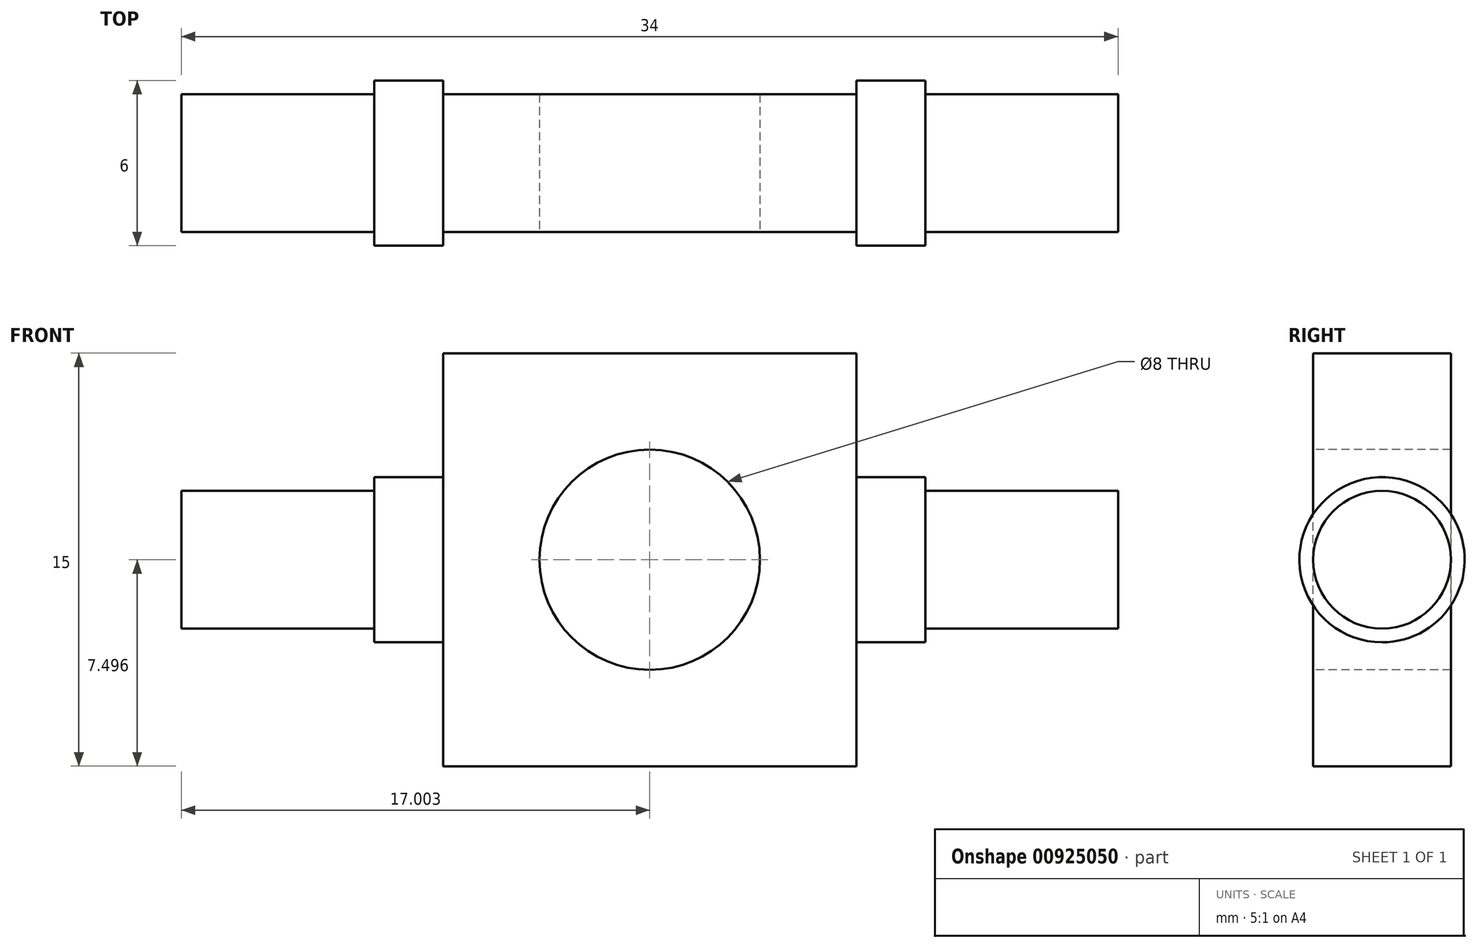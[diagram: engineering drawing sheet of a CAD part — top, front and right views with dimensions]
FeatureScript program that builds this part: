
annotation { "Feature Type Name" : "Feature", "Feature Type Description" : "" }
export const myFeature = defineFeature(function(context is Context, id is Id, definition is map)
    precondition{}
    {
        {
            var Q0;
            Q0=qCreatedBy(makeId("Front.planeOp"),FACE);
            var sketch = newSketch(context, id + "F0", { "sketchPlane" : qUnion([Q0])});
            skLineSegment(sketch, "E0.bottom", {"start": v(-9.98, 13.04) * mm, "end": v(5.02, 13.04) * mm});
            skLineSegment(sketch, "E0.top", {"start": v(-9.98, -1.96) * mm, "end": v(5.02, -1.96) * mm});
            skLineSegment(sketch, "E0.left", {"start": v(-9.98, 13.04) * mm, "end": v(-9.98, -1.96) * mm});
            skLineSegment(sketch, "E0.right", {"start": v(5.02, 13.04) * mm, "end": v(5.02, -1.96) * mm});
            skSolve(sketch);
        }
        {
            var Q0;
            Q0=makeQuery(id+"F0.imprint","IMPRINT",FACE,{"disambiguationData":[TD([[makeQuery(id+"F0.imprint","IMPRINT",EDGE,{"derivedFrom":sQuery(id+"F0.wireOp",EDGE,"E0.bottom")}),-1.0]])]});
            extrude(context, id + "F1", {"entities" : qUnion([Q0]), "depth" : 5 * mm, "offsetDistance" : 25 * mm});
        }
        {
            var Q0;
            Q0=makeQuery(id+"F1.opExtrude","CAP_FACE",FACE,{"disambiguationData":[OSD([sQuery(id+"F0.wireOp",EDGE,"E0.bottom"),sQuery(id+"F0.wireOp",EDGE,"E0.top"),sQuery(id+"F0.wireOp",EDGE,"E0.left"),sQuery(id+"F0.wireOp",EDGE,"E0.right")])],"isStart":false});
            var sketch = newSketch(context, id + "F2", { "sketchPlane" : qUnion([Q0])});
            skCircle(sketch, "E1", {"center": v(-2.48, 5.54) * mm, "radius": 4 * mm});
            skSolve(sketch);
        }
        {
            var Q0;
            Q0=makeQuery(id+"F2.imprint","IMPRINT",FACE,{"disambiguationData":[TD([[makeQuery(id+"F2.imprint","IMPRINT",EDGE,{"derivedFrom":sQuery(id+"F2.wireOp",EDGE,"E1")}),1.0]])]});
            extrude(context, id + "F3", {"entities" : qUnion([Q0]), "operationType" : NewBodyOperationType.REMOVE, "oppositeDirection" : true, "depth" : 25 * mm, "offsetDistance" : 25 * mm});
        }
        {
            var Q0;
            Q0=makeQuery(id+"F1.opExtrude","SWEPT_FACE",FACE,{"disambiguationData":[OSD([sQuery(id+"F0.wireOp",EDGE,"E0.right")])]});
            var sketch = newSketch(context, id + "F4", { "sketchPlane" : qUnion([Q0])});
            skCircle(sketch, "E2", {"center": v(-2.5, 5.54) * mm, "radius": 3 * mm});
            skSolve(sketch);
        }
        {
            var Q0;
            Q0 = qSketchRegion(id + "F4", true);
            extrude(context, id + "F5", {"entities" : qUnion([Q0]), "operationType" : NewBodyOperationType.ADD, "depth" : 2.5 * mm, "offsetDistance" : 25 * mm});
        }
        {
            var Q0;
            Q0=makeQuery(id+"F1.opExtrude","CAP_EDGE",EDGE,{"disambiguationData":[OSD([sQuery(id+"F0.wireOp",EDGE,"E0.bottom")])],"isStart":true});
            cPoint(context, id + "F6", {"entities" : qUnion([Q0]), "parameter" : 0.5});
        }
        {
            var Q0;
            Q0=makeQuery(id+"F1.opExtrude","CAP_EDGE",EDGE,{"disambiguationData":[OSD([sQuery(id+"F0.wireOp",EDGE,"E0.bottom")])],"isStart":false});
            cPoint(context, id + "F7", {"entities" : qUnion([Q0]), "parameter" : 0.5});
        }
        {
            var Q0;
            Q0=makeQuery(id+"F1.opExtrude","CAP_EDGE",EDGE,{"disambiguationData":[OSD([sQuery(id+"F0.wireOp",EDGE,"E0.top")])],"isStart":false});
            cPoint(context, id + "F8", {"entities" : qUnion([Q0]), "parameter" : 0.5});
        }
        {
            var Q0;
            Q0 = qCreatedBy(id + "F6" ,VERTEX);
            var Q1;
            Q1 = qCreatedBy(id + "F7" ,VERTEX);
            var Q2;
            Q2 = qCreatedBy(id + "F8" ,VERTEX);
            cPlane(context, id + "F9", {"entities" : qUnion([Q0, Q1, Q2]), "cplaneType" : CPlaneType.THREE_POINT, "offset" : 25 * mm, "width" : 150 * mm, "height" : 150 * mm});
        }
        {
            var Q0;
            Q0=makeQuery(id+"F5.opExtrude","CAP_FACE",FACE,{"disambiguationData":[OSD([sQuery(id+"F4.wireOp",EDGE,"E2")])],"isStart":false});
            var sketch = newSketch(context, id + "F10", { "sketchPlane" : qUnion([Q0])});
            skCircle(sketch, "E3", {"center": v(-2.5, 5.54) * mm, "radius": 2.5 * mm});
            skSolve(sketch);
        }
        {
            var Q0;
            Q0=makeQuery(id+"F10.imprint","IMPRINT",FACE,{"disambiguationData":[TD([[makeQuery(id+"F10.imprint","IMPRINT",EDGE,{"derivedFrom":sQuery(id+"F10.wireOp",EDGE,"E3")}),1.0]])]});
            extrude(context, id + "F11", {"entities" : qUnion([Q0]), "operationType" : NewBodyOperationType.ADD, "depth" : 7 * mm, "offsetDistance" : 25 * mm});
        }
        {
            var Q0;
            Q0=makeQuery(id+"F1.opExtrude","SWEPT_BODY",BODY,{"disambiguationData":[OSD([sQuery(id+"F0.wireOp",EDGE,"E0.bottom"),sQuery(id+"F0.wireOp",EDGE,"E0.top"),sQuery(id+"F0.wireOp",EDGE,"E0.left"),sQuery(id+"F0.wireOp",EDGE,"E0.right")])]});
            var Q1;
            Q1=qCreatedBy(id+"F9.planeOp",FACE);
            mirror(context, id + "F12", {"operationType" : NewBodyOperationType.ADD, "entities" : qUnion([Q0]), "mirrorPlane" : qUnion([Q1])});
        }
    });
